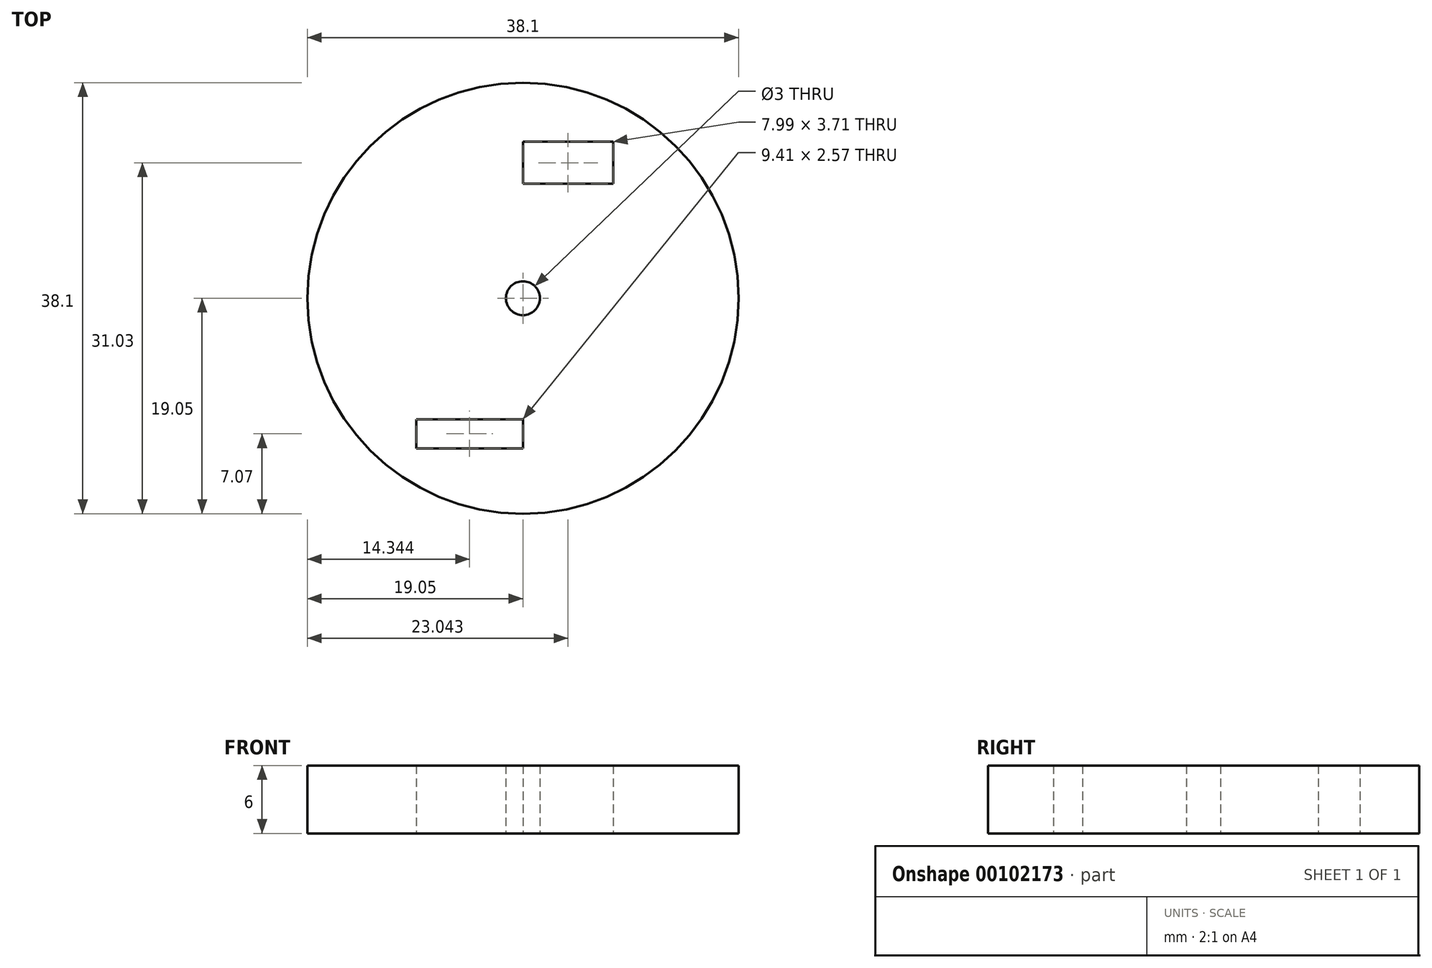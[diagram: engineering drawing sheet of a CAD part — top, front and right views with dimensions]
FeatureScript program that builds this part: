
annotation { "Feature Type Name" : "Feature", "Feature Type Description" : "" }
export const myFeature = defineFeature(function(context is Context, id is Id, definition is map)
    precondition{}
    {
        {
            var Q0;
            Q0=qCreatedBy(makeId("Top.planeOp"),FACE);
            var sketch = newSketch(context, id + "F0", { "sketchPlane" : qUnion([Q0])});
            skCircle(sketch, "E0", {"center": v(0, 0) * mm, "radius": 19.05 * mm});
            skCircle(sketch, "E1", {"center": v(0, 0) * mm, "radius": 1.5 * mm});
            skLineSegment(sketch, "E2.bottom", {"start": v(0, 13.83) * mm, "end": v(7.99, 13.83) * mm});
            skLineSegment(sketch, "E2.top", {"start": v(0, 10.13) * mm, "end": v(7.99, 10.13) * mm});
            skLineSegment(sketch, "E2.left", {"start": v(0, 13.83) * mm, "end": v(0, 10.13) * mm});
            skLineSegment(sketch, "E2.right", {"start": v(7.99, 13.83) * mm, "end": v(7.99, 10.13) * mm});
            skLineSegment(sketch, "E3.bottom", {"start": v(-9.41, -10.7) * mm, "end": v(0, -10.7) * mm});
            skLineSegment(sketch, "E3.top", {"start": v(-9.41, -13.26) * mm, "end": v(0, -13.26) * mm});
            skLineSegment(sketch, "E3.left", {"start": v(-9.41, -10.7) * mm, "end": v(-9.41, -13.26) * mm});
            skLineSegment(sketch, "E3.right", {"start": v(0, -10.7) * mm, "end": v(0, -13.26) * mm});
            skSolve(sketch);
        }
        {
            var Q0;
            Q0=makeQuery(id+"F0.imprint","IMPRINT",FACE,{"disambiguationData":[TD([[makeQuery(id+"F0.imprint","IMPRINT",EDGE,{"derivedFrom":sQuery(id+"F0.wireOp",EDGE,"E0")}),1.0]])]});
            extrude(context, id + "F1", {"entities" : qUnion([Q0]), "depth" : 6 * mm});
        }
    });
